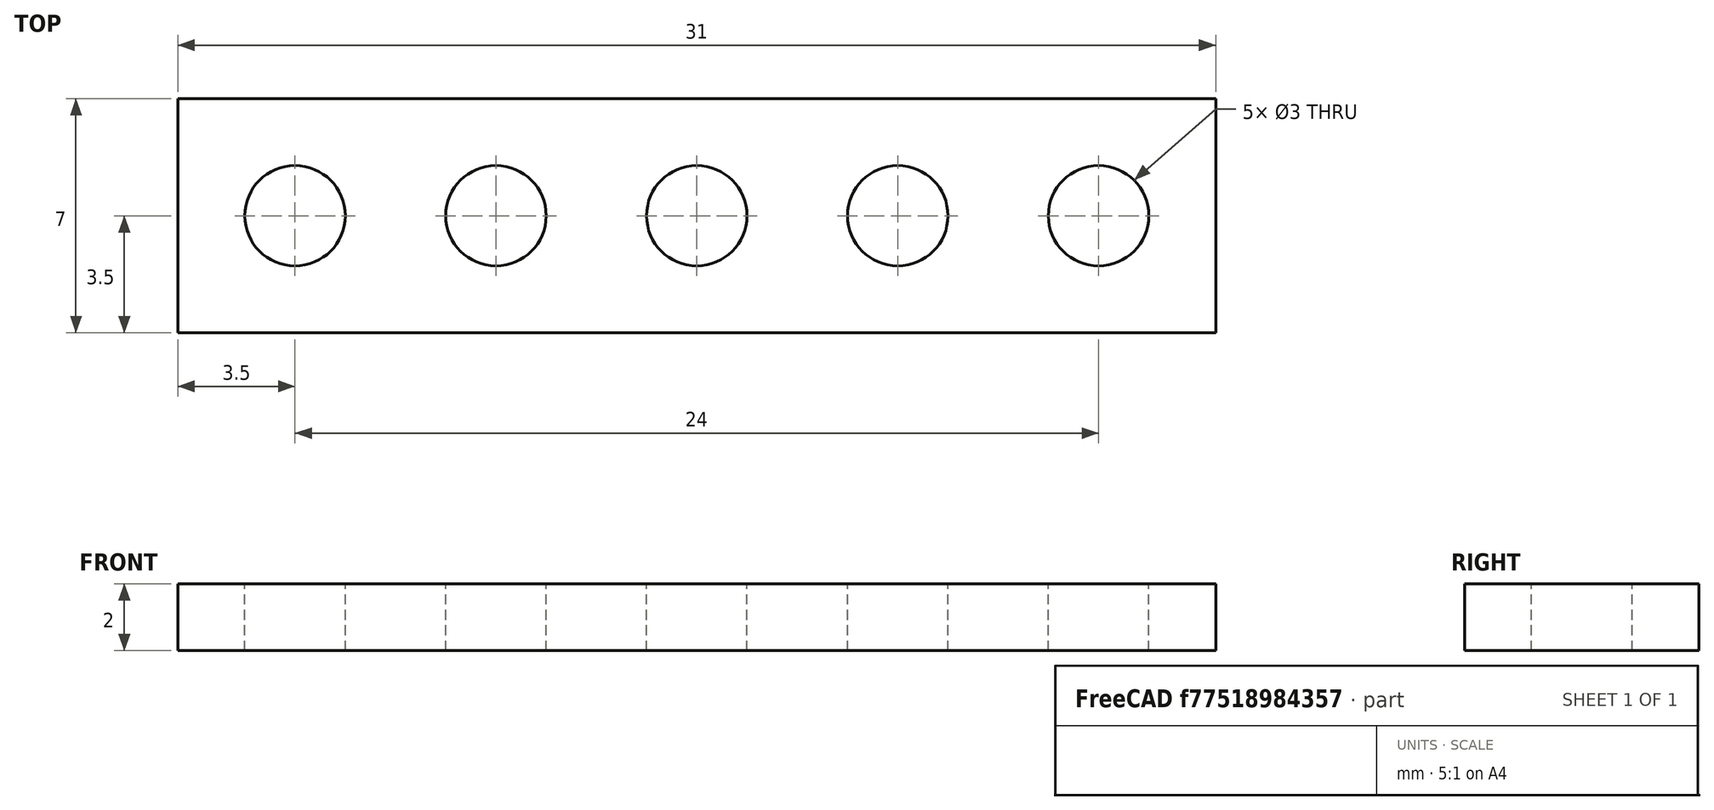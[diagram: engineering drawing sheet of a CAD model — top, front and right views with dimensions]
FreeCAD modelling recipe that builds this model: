
FCSTD DOCUMENT  (FreeCAD 0.18.4R)
Label: tutorial_freecad_ex10_b
License: All rights reserved
LicenseURL: http://en.wikipedia.org/wiki/All_rights_reserved
objects: Part::Cylinder×1, Part::FeaturePython×1, Part::Box×1, Part::Cut×1
note: 4 computed .brp shape members not serialized (recipe doc carries the construction recipe); baked Part::Feature solids carry a one-line shape summary decoded from their .brp

FEATURE [Part::Cylinder] Cylinder  label="Cilindro"
  Angle = 360
  AttacherType = Attacher::AttachEngine3D
  Height = 4
  Radius = 1.5
FEATURE [Part::FeaturePython] Array  label="buracos"  # Draft array (typed FeaturePython)
  Angle = 360
  ArrayType = 0
  Axis = (0,0,1)
  Base = -> Cylinder
  Center = (0,0,0)
  Fuse = false
  IntervalAxis = (0,0,0)
  IntervalX = (6,0,0)
  IntervalY = (0,1,0)
  IntervalZ = (0,0,1)
  NumberPolar = 1
  NumberX = 5
  NumberY = 1
  NumberZ = 1
  Placement = pos=(3.5,3.5,0) rot=(0,0,1;0rad)
FEATURE [Part::Box] Box  label="base"
  AttacherType = Attacher::AttachEngine3D
  Height = 2
  Length = 31
  Width = 7
FEATURE [Part::Cut] Cut
  Base = -> Box
  Refine = true
  Tool = -> Array
